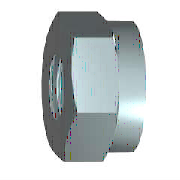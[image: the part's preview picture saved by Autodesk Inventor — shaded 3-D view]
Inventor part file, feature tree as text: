
AUTODESK INVENTOR PART (.ipt)
format: ipt  version: 2015 (Build 190159000, 159)  size: 193,024 bytes
history: native  units: mm (DEFAULTED — no unit token found)
features: sketch x4, extrude x1, chamfer x1, hole x1, other x1, plane x1, fillet x1
ambient origin geometry x7: Origin, YZ Plane, XZ Plane, X Axis, Y Axis, Z Axis, Center Point
bodies: Solid1 (feature_tree), Body (feature_tree)
feature tree (10):
  extrude  "Ring"  Depth=2.15mm
  chamfer  "Chamfer1"  Distance=4.57mm
  hole  "Thread"  [1 undecoded]
  other  "Work Axis1"
  plane  "Work Plane1"
  fillet  "Fillet1"  [1 undecoded]
  sketch  "Sketch1"  dims[d0=6.350853mm d1=2.15mm]
  sketch  "Sketch3"  dims[d3=30.0deg]
  sketch  "Sketch2"  dims[d2=0.0mm]
  sketch  "Sketch4"  dims[d4=30.0deg d5=4.57mm d6=4.57mm d26=90.0deg d7=4.57mm d8=2.35mm d9=0.0mm d30=2.459mm d31=6.0mm d32=4.0mm d33=2.0mm d34=14.3117mm d35=8.0mm d36=20.594885mm d10=0.270633mm d11=30.0deg d12=0.270633mm d13=30.0deg d14=0.0mm d15=0.0mm d45=0.0mm d46=0.270633mm d47=0.270633mm d48=0.0mm d49=0.7mm]
note: 2 required parameter values undecoded (feature->parameter linkage not recoverable at this tier; creation-order binding heuristic only, values carry confidence <= 0.55)
